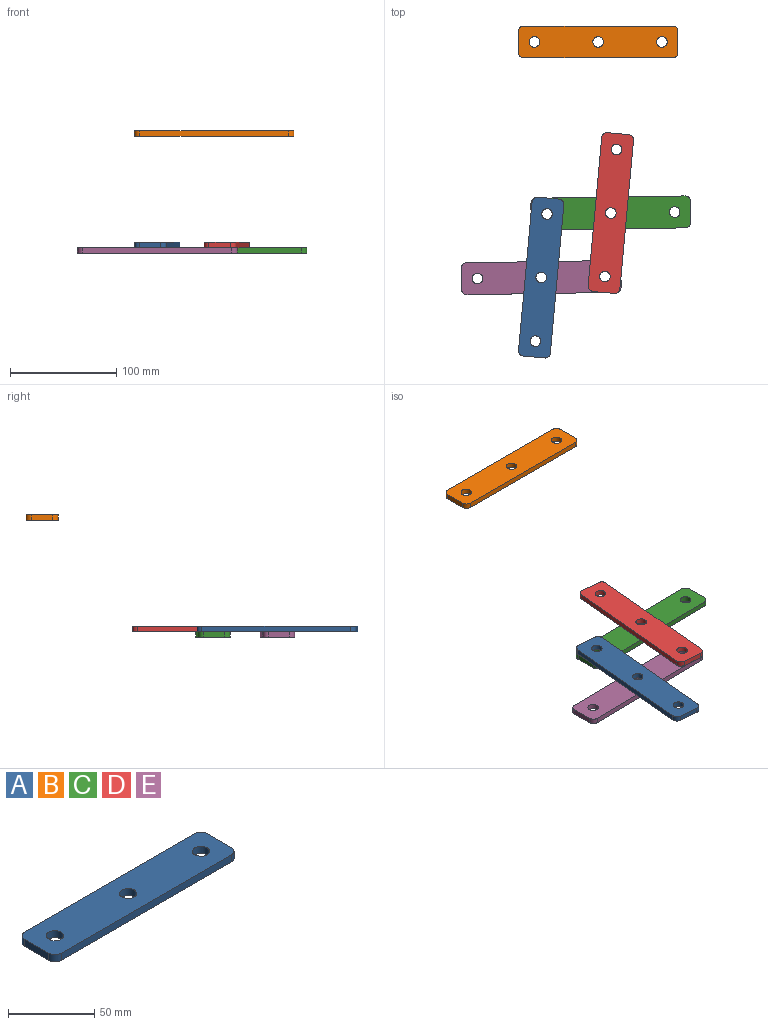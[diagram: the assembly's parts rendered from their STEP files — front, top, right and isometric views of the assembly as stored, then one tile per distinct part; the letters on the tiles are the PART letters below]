
ASSEMBLY  parts=5 mates=4
PART A: 13 faces, bbox 150x30x5 mm
  f0: plane 140x5mm, normal (0,1,0), area 700mm2, adj f1,f10,f11,f12
  f1: cylinder r=5mm len=5mm, axis (0,0,-1), area 39.3mm2, adj f0,f2,f11,f12
  f2: plane 20x5mm, normal (-1,0,0), area 100mm2, adj f1,f3,f11,f12
  f3: cylinder r=5mm len=5mm, axis (0,0,-1), area 39.3mm2, adj f2,f4,f11,f12
  f4: plane 140x5mm, normal (0,-1,0), area 700mm2, adj f3,f5,f11,f12
  f5: cylinder r=5mm len=5mm, axis (0,0,-1), area 39.3mm2, adj f4,f6,f11,f12
  f6: plane 20x5mm, normal (1,0,0), area 100mm2, adj f5,f10,f11,f12
  f7: cylinder r=5mm len=10mm, axis (0,0,-1), area 157.1mm2, adj f11,f12
  f8: cylinder r=5mm len=10mm, axis (0,0,-1), area 157.1mm2, adj f11,f12
  f9: cylinder r=5mm len=10mm, axis (0,0,-1), area 157.1mm2, adj f11,f12
  f10: cylinder r=5mm len=5mm, axis (0,0,-1), area 39.3mm2, adj f0,f6,f11,f12
  f11: plane 150x30mm, normal (0,0,1), area 4242.9mm2, adj f0,f1,f2,f3,f4,f5,f6,f7
  f12: plane 150x30mm, normal (0,0,-1), area 4242.9mm2, adj f0,f1,f2,f3,f4,f5,f6,f7
PART B: same geometry as A
PART C: same geometry as A
PART D: same geometry as A
PART E: same geometry as A
PLACE A rot(axis=(0,0,-1),95.2deg) t=(-42.45,-196.04,-79.06)mm
PLACE B t=(11.16,25.32,25.81)mm
PLACE C rot(axis=(0,0,1),0.9deg) t=(23.02,-135.36,-84.06)mm fixed
PLACE D rot(axis=(0,0,1),84.8deg) t=(23.02,-135.36,-79.06)mm
PLACE E rot(axis=(0,0,1),0.9deg) t=(-42.45,-196.04,-84.06)mm
MATE revolute D.f8 <-> C.f8  axis (0,0,-1) through (23.02,-135.36,-79.06)mm
MATE revolute E.f9 <-> D.f7  axis (0,0,1) through (17.55,-195.11,-79.06)mm
MATE revolute E.f8 <-> A.f8  axis (0,0,1) through (-42.45,-196.04,-79.06)mm
MATE revolute A.f7 <-> C.f7  axis (0,0,-1) through (-36.97,-136.29,-79.06)mm
